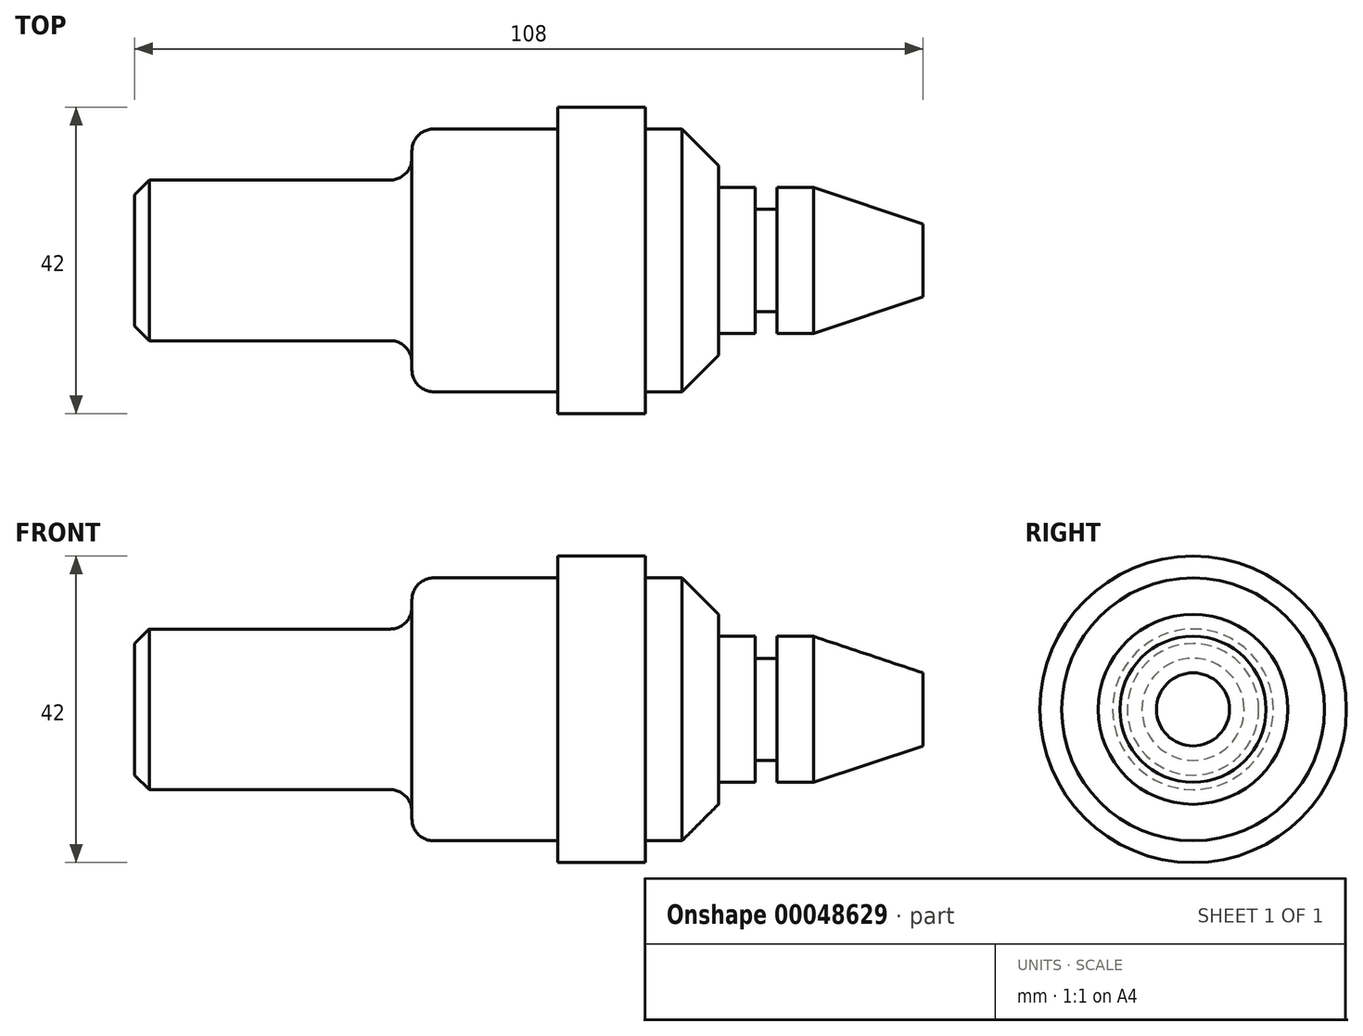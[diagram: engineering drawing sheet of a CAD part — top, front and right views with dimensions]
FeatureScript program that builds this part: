
annotation { "Feature Type Name" : "Feature", "Feature Type Description" : "" }
export const myFeature = defineFeature(function(context is Context, id is Id, definition is map)
    precondition{}
    {
        {
            var Q0;
            Q0=qCreatedBy(makeId("Top.planeOp"),FACE);
            var sketch = newSketch(context, id + "F0", { "sketchPlane" : qUnion([Q0])});
            skLineSegment(sketch, "E0", {"start": v(-49.16, 0) * mm, "end": v(58.84, 0) * mm});
            skLineSegment(sketch, "E1", {"start": v(-49.16, 0) * mm, "end": v(-49.16, -11) * mm});
            skLineSegment(sketch, "E2", {"start": v(-49.16, -11) * mm, "end": v(-11.16, -11) * mm});
            skLineSegment(sketch, "E3", {"start": v(-11.16, -11) * mm, "end": v(-11.16, -18) * mm});
            skLineSegment(sketch, "E4", {"start": v(-11.16, -18) * mm, "end": v(8.84, -18) * mm});
            skLineSegment(sketch, "E5", {"start": v(8.84, -18) * mm, "end": v(8.84, -21) * mm});
            skLineSegment(sketch, "E6", {"start": v(8.84, -21) * mm, "end": v(20.84, -21) * mm});
            skLineSegment(sketch, "E7", {"start": v(20.84, -21) * mm, "end": v(20.84, -18) * mm});
            skLineSegment(sketch, "E8", {"start": v(20.84, -18) * mm, "end": v(30.84, -18) * mm});
            skLineSegment(sketch, "E9", {"start": v(30.84, -18) * mm, "end": v(30.84, -10) * mm});
            skLineSegment(sketch, "E10", {"start": v(30.84, -10) * mm, "end": v(35.84, -10) * mm});
            skLineSegment(sketch, "E11", {"start": v(38.84, -10) * mm, "end": v(43.84, -10) * mm});
            skLineSegment(sketch, "E12", {"start": v(43.84, -10) * mm, "end": v(58.84, -5) * mm});
            skLineSegment(sketch, "E13", {"start": v(58.84, 0) * mm, "end": v(58.84, -5) * mm});
            skLineSegment(sketch, "E14", {"start": v(35.84, -10) * mm, "end": v(35.84, -7) * mm});
            skLineSegment(sketch, "E15", {"start": v(35.84, -7) * mm, "end": v(38.84, -7) * mm});
            skLineSegment(sketch, "E16", {"start": v(38.84, -10) * mm, "end": v(38.84, -7) * mm});
            skSolve(sketch);
        }
        {
            var Q0;
            Q0=makeQuery(id+"F0.imprint","IMPRINT",FACE,{"disambiguationData":[TD([[makeQuery(id+"F0.imprint","IMPRINT",EDGE,{"derivedFrom":sQuery(id+"F0.wireOp",EDGE,"E0")}),-1.0]])]});
            var Q1;
            Q1=sQuery(id+"F0.wireOp",EDGE,"E0");
            revolve(context, id + "F1", {"entities" : qUnion([Q0]), "axis" : qUnion([Q1]), "revolveType" : RevolveType.FULL});
        }
        {
            var Q0;
            Q0=makeQuery(id+"F1.opRevolve","SWEPT_EDGE",EDGE,{"disambiguationData":[OSD([sQuery(id+"F0.wireOp",EDGE,"E1"),sQuery(id+"F0.wireOp",EDGE,"E2")])]});
            chamfer(context, id + "F2", {"entities" : qUnion([Q0]), "chamferType" : ChamferType.OFFSET_ANGLE, "width" : 2 * mm, "oppositeDirection" : false, "angle" : 45 * degree, "tangentPropagation" : true});
        }
        {
            var Q0;
            Q0=makeQuery(id+"F1.opRevolve","SWEPT_EDGE",EDGE,{"disambiguationData":[OSD([sQuery(id+"F0.wireOp",EDGE,"E8"),sQuery(id+"F0.wireOp",EDGE,"E9")])]});
            chamfer(context, id + "F3", {"entities" : qUnion([Q0]), "width" : 5 * mm, "tangentPropagation" : true});
        }
        {
            var Q0;
            Q0=makeQuery(id+"F1.opRevolve","SWEPT_EDGE",EDGE,{"disambiguationData":[OSD([sQuery(id+"F0.wireOp",EDGE,"E3"),sQuery(id+"F0.wireOp",EDGE,"E4")])]});
            var Q1;
            Q1=makeQuery(id+"F1.opRevolve","SWEPT_FACE",FACE,{"disambiguationData":[OSD([sQuery(id+"F0.wireOp",EDGE,"E3")])]});
            fillet(context, id + "F4", {"entities" : qUnion([Q0, Q1]), "radius" : 3 * mm, "tangentPropagation" : true, "allowEdgeOverflow" : false});
        }
    });
